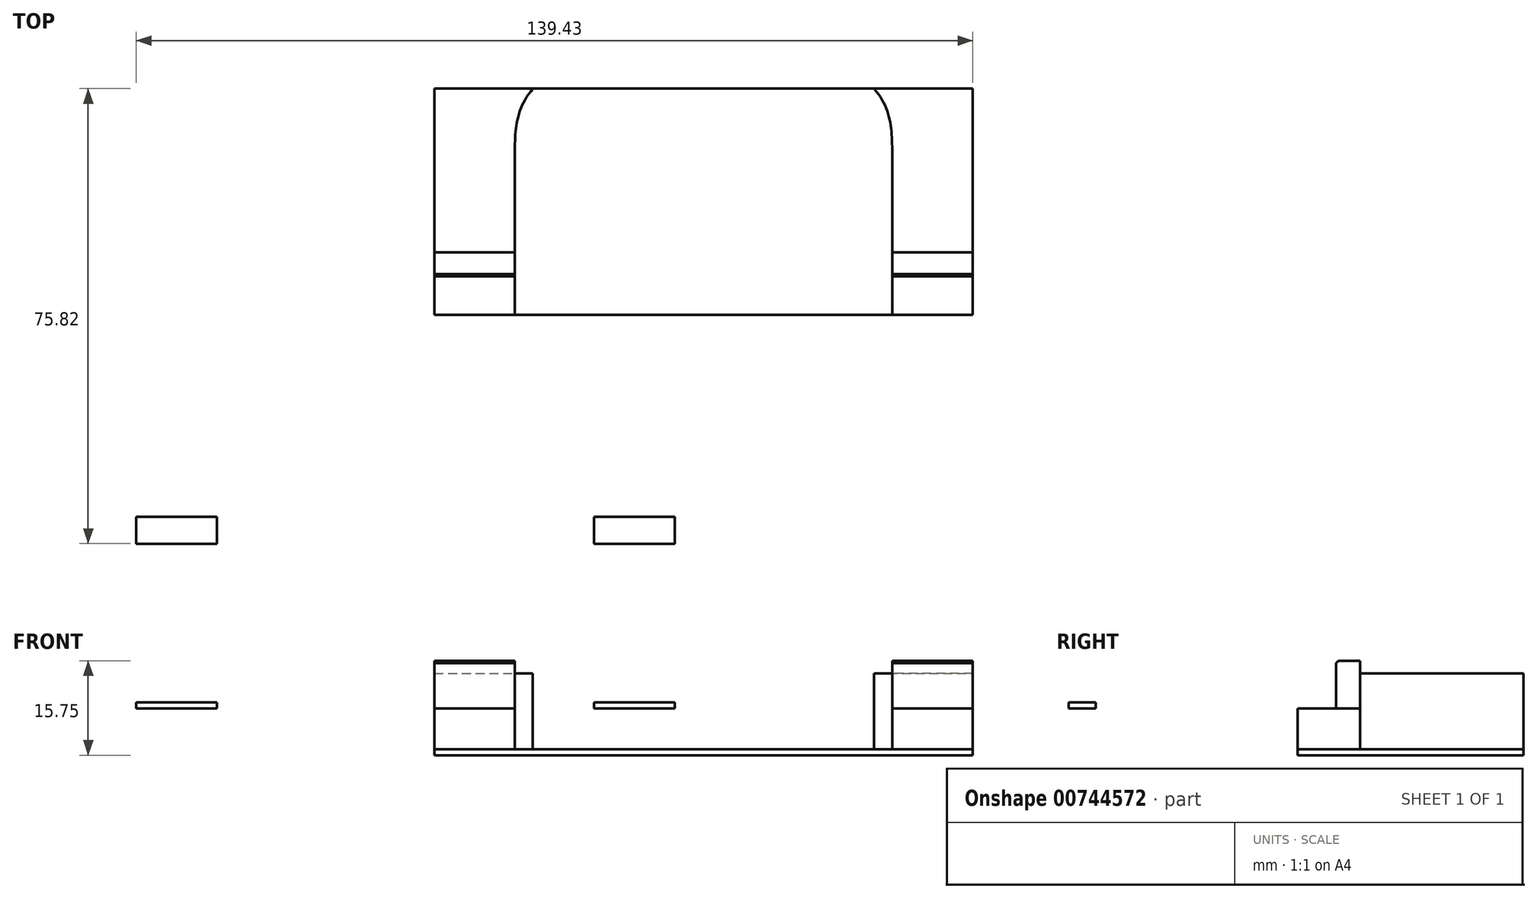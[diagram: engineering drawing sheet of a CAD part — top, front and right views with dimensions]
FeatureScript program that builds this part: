
annotation { "Feature Type Name" : "Feature", "Feature Type Description" : "" }
export const myFeature = defineFeature(function(context is Context, id is Id, definition is map)
    precondition{}
    {
        {
            assignVariable(context, id + "F0", {"name" : "ks_do_riser_height", "anyValue" : 8.95});
        }
        {
            var Q0;
            Q0=qCreatedBy(makeId("Top.planeOp"),FACE);
            var sketch = newSketch(context, id + "F1", { "sketchPlane" : qUnion([Q0])});
            skLineSegment(sketch, "E0", {"start": v(-49.68, -38.15) * mm, "end": v(40.07, -38.15) * mm});
            skPoint(sketch, "E1", {"position": v(-4.8, -38.15) * mm});
            skPoint(sketch, "E2", {"position": v(26.64, -38.15) * mm});
            skPoint(sketch, "E3", {"position": v(-36.26, -38.15) * mm});
            skPoint(sketch, "E4", {"position": v(-49.68, -33.65) * mm});
            skLineSegment(sketch, "E5", {"start": v(-49.68, -38.15) * mm, "end": v(-49.68, -33.65) * mm});
            skLineSegment(sketch, "E6", {"start": v(-49.68, -33.65) * mm, "end": v(-36.26, -33.65) * mm});
            skLineSegment(sketch, "E7", {"start": v(-36.26, -33.65) * mm, "end": v(-36.26, -38.15) * mm});
            skLineSegment(sketch, "E8", {"start": v(26.64, -38.15) * mm, "end": v(26.64, -33.65) * mm});
            skLineSegment(sketch, "E9", {"start": v(26.64, -33.65) * mm, "end": v(40.07, -33.65) * mm});
            skLineSegment(sketch, "E10", {"start": v(40.07, -33.65) * mm, "end": v(40.07, -38.15) * mm});
            skSolve(sketch);
        }
        {
            var Q0;
            {var subQ0=sQuery(id+"F1.wireOp",EDGE,"E5");Q0=makeQuery(id+"F1.imprint","IMPRINT",FACE,{"disambiguationData":[TD([[makeQuery(id+"F1.imprint","IMPRINT",EDGE,{"derivedFrom":subQ0}),-1.0]])]});}
            var Q1;
            {var subQ2=sQuery(id+"F1.wireOp",EDGE,"E8");Q1=makeQuery(id+"F1.imprint","IMPRINT",FACE,{"disambiguationData":[TD([[makeQuery(id+"F1.imprint","IMPRINT",EDGE,{"derivedFrom":subQ2}),-1.0]])]});}
            extrude(context, id + "F2", {"entities" : qUnion([Q0, Q1]), "depth" : 1 * mm, "offsetDistance" : 25 * mm});
        }
        {
            var Q0;
            Q0=makeQuery(id+"F2.opExtrude","CAP_FACE",FACE,{"disambiguationData":[OSD([sQuery(id+"F1.wireOp",EDGE,"E0"),sQuery(id+"F1.wireOp",EDGE,"E5"),sQuery(id+"F1.wireOp",EDGE,"E6"),sQuery(id+"F1.wireOp",EDGE,"E7")])],"isStart":false});
            var sketch = newSketch(context, id + "F3", { "sketchPlane" : qUnion([Q0])});
            skLineSegment(sketch, "E11", {"start": v(-49.68, -38.15) * mm, "end": v(-49.68, -34.15) * mm});
            skLineSegment(sketch, "E12", {"start": v(-49.68, -34.15) * mm, "end": v(-36.26, -34.15) * mm});
            skLineSegment(sketch, "E13", {"start": v(-36.26, -34.15) * mm, "end": v(-36.26, -38.15) * mm});
            skLineSegment(sketch, "E14", {"start": v(-36.26, -38.15) * mm, "end": v(-49.68, -38.15) * mm});
            skPoint(sketch, "E15", {"position": v(40.07, -38.15) * mm});
            skPoint(sketch, "E16", {"position": v(26.64, -34.15) * mm});
            skLineSegment(sketch, "E17.bottom", {"start": v(26.64, -34.15) * mm, "end": v(40.07, -34.15) * mm});
            skLineSegment(sketch, "E17.top", {"start": v(26.64, -38.15) * mm, "end": v(40.07, -38.15) * mm});
            skLineSegment(sketch, "E17.left", {"start": v(26.64, -34.15) * mm, "end": v(26.64, -38.15) * mm});
            skLineSegment(sketch, "E17.right", {"start": v(40.07, -34.15) * mm, "end": v(40.07, -38.15) * mm});
            skSolve(sketch);
        }
        {
            var Q0;
            Q0=makeQuery(id+"F3.imprint","IMPRINT",FACE,{"disambiguationData":[TD([[makeQuery(id+"F3.imprint","IMPRINT",EDGE,{"derivedFrom":sQuery(id+"F3.wireOp",EDGE,"E11")}),-1.0]])]});
            var Q1;
            Q1=makeQuery(id+"F3.imprint","IMPRINT",FACE,{"disambiguationData":[TD([[makeQuery(id+"F3.imprint","IMPRINT",EDGE,{"derivedFrom":sQuery(id+"F3.wireOp",EDGE,"E17.bottom")}),-1.0]])]});
            extrude(context, id + "F4", {"entities" : qUnion([Q0, Q1]), "depth" : (getVariable(context, 'ks_do_riser_height') - 1) * mm, "offsetDistance" : 25 * mm});
        }
        {
            var Q0;
            Q0=makeQuery(id+"F4.opExtrude","CAP_FACE",FACE,{"disambiguationData":[OSD([sQuery(id+"F3.wireOp",EDGE,"E11"),sQuery(id+"F3.wireOp",EDGE,"E12"),sQuery(id+"F3.wireOp",EDGE,"E13"),sQuery(id+"F3.wireOp",EDGE,"E14")])],"isStart":false});
            var sketch = newSketch(context, id + "F5", { "sketchPlane" : qUnion([Q0])});
            skLineSegment(sketch, "E18.bottom", {"start": v(-49.68, -38.15) * mm, "end": v(-36.26, -38.15) * mm});
            skLineSegment(sketch, "E18.top", {"start": v(-49.68, -27.75) * mm, "end": v(-36.26, -27.75) * mm});
            skLineSegment(sketch, "E18.left", {"start": v(-49.68, -38.15) * mm, "end": v(-49.68, -27.75) * mm});
            skLineSegment(sketch, "E18.right", {"start": v(-36.26, -38.15) * mm, "end": v(-36.26, -27.75) * mm});
            skPoint(sketch, "E19", {"position": v(26.64, -38.15) * mm});
            skPoint(sketch, "E20", {"position": v(40.07, -27.75) * mm});
            skLineSegment(sketch, "E21.bottom", {"start": v(26.64, -38.15) * mm, "end": v(40.07, -38.15) * mm});
            skLineSegment(sketch, "E21.top", {"start": v(26.64, -27.75) * mm, "end": v(40.07, -27.75) * mm});
            skLineSegment(sketch, "E21.left", {"start": v(26.64, -38.15) * mm, "end": v(26.64, -27.75) * mm});
            skLineSegment(sketch, "E21.right", {"start": v(40.07, -38.15) * mm, "end": v(40.07, -27.75) * mm});
            skSolve(sketch);
        }
        {
            var Q0;
            Q0=makeQuery(id+"F5.imprint","IMPRINT",FACE,{"disambiguationData":[TD([[makeQuery(id+"F5.imprint","IMPRINT",EDGE,{"derivedFrom":sQuery(id+"F5.wireOp",EDGE,"E21.bottom")}),1.0]])]});
            var Q1;
            {var subQ0=sQuery(id+"F5.wireOp",EDGE,"E18.top");Q1=makeQuery(id+"F5.imprint","IMPRINT",FACE,{"disambiguationData":[TD([[makeQuery(id+"F5.imprint","IMPRINT",EDGE,{"derivedFrom":subQ0}),-1.0]])]});}
            var Q2;
            {var subQ0=sQuery(id+"F5.wireOp",EDGE,"E18.bottom");Q2=makeQuery(id+"F5.imprint","IMPRINT",FACE,{"disambiguationData":[TD([[makeQuery(id+"F5.imprint","IMPRINT",EDGE,{"derivedFrom":subQ0}),1.0]])]});}
            extrude(context, id + "F6", {"entities" : qUnion([Q0, Q1, Q2]), "depth" : 6.8 * mm, "offsetDistance" : 25 * mm});
        }
        {
            var Q0;
            Q0=makeQuery(id+"F6.opExtrude","CAP_FACE",FACE,{"disambiguationData":[OSD([sQuery(id+"F5.wireOp",EDGE,"E18.bottom"),sQuery(id+"F5.wireOp",EDGE,"E18.top"),sQuery(id+"F5.wireOp",EDGE,"E18.left"),sQuery(id+"F5.wireOp",EDGE,"E18.right")])],"isStart":false});
            var sketch = newSketch(context, id + "F7", { "sketchPlane" : qUnion([Q0])});
            skPoint(sketch, "E22", {"position": v(-49.68, -65.42) * mm});
            skPoint(sketch, "E23", {"position": v(40.07, -27.75) * mm});
            skLineSegment(sketch, "E24.bottom", {"start": v(-49.68, -65.42) * mm, "end": v(40.07, -65.42) * mm});
            skLineSegment(sketch, "E24.top", {"start": v(-49.68, -27.75) * mm, "end": v(40.07, -27.75) * mm});
            skLineSegment(sketch, "E24.left", {"start": v(-49.68, -65.42) * mm, "end": v(-49.68, -27.75) * mm});
            skLineSegment(sketch, "E24.right", {"start": v(40.07, -65.42) * mm, "end": v(40.07, -27.75) * mm});
            skSolve(sketch);
        }
        {
            var Q0;
            Q0 = qSketchRegion(id + "F7", true);
            extrude(context, id + "F8", {"entities" : qUnion([Q0]), "depth" : 1 * mm, "offsetDistance" : 25 * mm});
        }
        {
            var Q0;
            Q0=makeQuery(id+"F8.opExtrude","CAP_FACE",FACE,{"disambiguationData":[OSD([sQuery(id+"F7.wireOp",EDGE,"E24.bottom"),sQuery(id+"F7.wireOp",EDGE,"E24.top"),sQuery(id+"F7.wireOp",EDGE,"E24.left"),sQuery(id+"F7.wireOp",EDGE,"E24.right")])],"isStart":true});
            var sketch = newSketch(context, id + "F9", { "sketchPlane" : qUnion([Q0])});
            skPoint(sketch, "E25", {"position": v(26.64, 65.42) * mm});
            skPoint(sketch, "E26", {"position": v(23.64, 65.42) * mm});
            skPoint(sketch, "E27", {"position": v(26.64, 54.25) * mm});
            skPoint(sketch, "E28", {"position": v(40.07, 38.15) * mm});
            skLineSegment(sketch, "E29.bottom", {"start": v(40.07, 38.15) * mm, "end": v(26.64, 38.15) * mm});
            skLineSegment(sketch, "E29.top", {"start": v(40.07, 65.42) * mm, "end": v(26.64, 65.42) * mm});
            skLineSegment(sketch, "E29.left", {"start": v(40.07, 38.15) * mm, "end": v(40.07, 65.42) * mm});
            skLineSegment(sketch, "E29.right", {"start": v(26.64, 38.15) * mm, "end": v(26.64, 65.42) * mm});
            skFitSpline(sketch, "E30", {"points": [v(26.64, 54.25) * mm, v(23.64, 65.42) * mm], "startDerivative": vector(0, 11.66) * mm, "endDerivative": vector(-9, 10.44) * mm});
            skLineSegment(sketch, "E31", {"start": v(-4.8, 27.75) * mm, "end": v(-4.8, 67.87) * mm, "construction": true});
            skLineSegment(sketch, "E32", {"start": v(23.64, 65.42) * mm, "end": v(26.64, 65.42) * mm});
            skFitSpline(sketch, "E33.MirrorCS", {"points": [v(-36.26, 54.25) * mm, v(-33.26, 65.42) * mm], "startDerivative": vector(0, 11.66) * mm, "endDerivative": vector(9, 10.44) * mm});
            skLineSegment(sketch, "E34.MirrorCS", {"start": v(-33.26, 65.42) * mm, "end": v(-36.26, 65.42) * mm});
            skLineSegment(sketch, "E35.MirrorCS", {"start": v(-36.26, 38.15) * mm, "end": v(-36.26, 65.42) * mm});
            skLineSegment(sketch, "E36.MirrorCS", {"start": v(-49.68, 38.15) * mm, "end": v(-49.68, 65.42) * mm});
            skLineSegment(sketch, "E37.MirrorCS", {"start": v(-49.68, 38.15) * mm, "end": v(-36.26, 38.15) * mm});
            skLineSegment(sketch, "E38.MirrorCS", {"start": v(-49.68, 65.42) * mm, "end": v(-36.26, 65.42) * mm});
            skSolve(sketch);
        }
        {
            var Q0;
            Q0=makeQuery(id+"F9.imprint","IMPRINT",FACE,{"disambiguationData":[TD([[makeQuery(id+"F9.imprint","IMPRINT",EDGE,{"derivedFrom":sQuery(id+"F9.wireOp",EDGE,"E36.MirrorCS")}),1.0]])]});
            var Q1;
            {var subQ2=sQuery(id+"F9.wireOp",EDGE,"E30");Q1=makeQuery(id+"F9.imprint","IMPRINT",FACE,{"disambiguationData":[TD([[makeQuery(id+"F9.imprint","IMPRINT",EDGE,{"derivedFrom":subQ2}),-1.0]])]});}
            var Q2;
            {var subQ1=sQuery(id+"F9.wireOp",EDGE,"E29.bottom");Q2=makeQuery(id+"F9.imprint","IMPRINT",FACE,{"disambiguationData":[TD([[makeQuery(id+"F9.imprint","IMPRINT",EDGE,{"derivedFrom":subQ1}),-1.0]])]});}
            var Q3;
            {var subQ0=sQuery(id+"F9.wireOp",EDGE,"E33.MirrorCS");Q3=makeQuery(id+"F9.imprint","IMPRINT",FACE,{"disambiguationData":[TD([[makeQuery(id+"F9.imprint","IMPRINT",EDGE,{"derivedFrom":subQ0}),1.0]])]});}
            extrude(context, id + "F10", {"entities" : qUnion([Q0, Q1, Q2, Q3]), "depth" : 12.6 * mm, "offsetDistance" : 25 * mm});
        }
        {
            var Q0;
            Q0=makeQuery(id+"F4.opExtrude","CAP_EDGE",EDGE,{"disambiguationData":[OSD([sQuery(id+"F3.wireOp",EDGE,"E12")])],"isStart":true});
            chamfer(context, id + "F11", {"entities" : qUnion([Q0]), "width" : 0.4 * mm, "tangentPropagation" : true});
        }
        {
            var Q0;
            Q0=makeQuery(id+"F4.opExtrude","CAP_EDGE",EDGE,{"disambiguationData":[OSD([sQuery(id+"F3.wireOp",EDGE,"E17.bottom")])],"isStart":true});
            chamfer(context, id + "F12", {"entities" : qUnion([Q0]), "width" : 0.4 * mm, "tangentPropagation" : true});
        }
        {
            var Q0;
            Q0=makeQuery(id+"F4.opExtrude","SWEPT_BODY",BODY,{"disambiguationData":[OSD([sQuery(id+"F3.wireOp",EDGE,"E11"),sQuery(id+"F3.wireOp",EDGE,"E12"),sQuery(id+"F3.wireOp",EDGE,"E13"),sQuery(id+"F3.wireOp",EDGE,"E14")])]});
            var Q1;
            Q1=makeQuery(id+"F4.opExtrude","SWEPT_BODY",BODY,{"disambiguationData":[OSD([sQuery(id+"F3.wireOp",EDGE,"E17.bottom"),sQuery(id+"F3.wireOp",EDGE,"E17.top"),sQuery(id+"F3.wireOp",EDGE,"E17.left"),sQuery(id+"F3.wireOp",EDGE,"E17.right")])]});
            var Q2;
            Q2=makeQuery(id+"F6.opExtrude","SWEPT_BODY",BODY,{"disambiguationData":[OSD([sQuery(id+"F5.wireOp",EDGE,"E18.bottom"),sQuery(id+"F5.wireOp",EDGE,"E18.top"),sQuery(id+"F5.wireOp",EDGE,"E18.left"),sQuery(id+"F5.wireOp",EDGE,"E18.right")])]});
            var Q3;
            Q3=makeQuery(id+"F6.opExtrude","SWEPT_BODY",BODY,{"disambiguationData":[OSD([sQuery(id+"F5.wireOp",EDGE,"E21.bottom"),sQuery(id+"F5.wireOp",EDGE,"E21.top"),sQuery(id+"F5.wireOp",EDGE,"E21.left"),sQuery(id+"F5.wireOp",EDGE,"E21.right")])]});
            var Q4;
            Q4=makeQuery(id+"F8.opExtrude","SWEPT_BODY",BODY,{"disambiguationData":[OSD([sQuery(id+"F7.wireOp",EDGE,"E24.bottom"),sQuery(id+"F7.wireOp",EDGE,"E24.top"),sQuery(id+"F7.wireOp",EDGE,"E24.left"),sQuery(id+"F7.wireOp",EDGE,"E24.right")])]});
            var Q5;
            Q5=makeQuery(id+"F10.opExtrude","SWEPT_BODY",BODY,{"disambiguationData":[OSD([sQuery(id+"F9.wireOp",EDGE,"E29.bottom"),sQuery(id+"F9.wireOp",EDGE,"E29.top"),sQuery(id+"F9.wireOp",EDGE,"E29.left"),sQuery(id+"F9.wireOp",EDGE,"E29.right"),sQuery(id+"F9.wireOp",EDGE,"E30"),sQuery(id+"F9.wireOp",EDGE,"E32")])]});
            var Q6;
            Q6=makeQuery(id+"F10.opExtrude","SWEPT_BODY",BODY,{"disambiguationData":[OSD([sQuery(id+"F9.wireOp",EDGE,"E33.MirrorCS"),sQuery(id+"F9.wireOp",EDGE,"E34.MirrorCS"),sQuery(id+"F9.wireOp",EDGE,"E35.MirrorCS"),sQuery(id+"F9.wireOp",EDGE,"E36.MirrorCS"),sQuery(id+"F9.wireOp",EDGE,"E37.MirrorCS"),sQuery(id+"F9.wireOp",EDGE,"E38.MirrorCS")])]});
            var Q7;
            Q7=makeQuery(id+"F8.opExtrude","CAP_EDGE",EDGE,{"disambiguationData":[OSD([sQuery(id+"F7.wireOp",EDGE,"E24.top")])],"isStart":false});
            transform(context, id + "F13", {"entities" : qUnion([Q0, Q1, Q2, Q3, Q4, Q5, Q6]), "transformType" : TransformType.ROTATION, "transformAxis" : qUnion([Q7]), "angle" : 180 * degree, "makeCopy" : false});
        }
        {
            var Q0;
            Q0=makeQuery(id+"F4.opExtrude","SWEPT_BODY",BODY,{"disambiguationData":[OSD([sQuery(id+"F3.wireOp",EDGE,"E11"),sQuery(id+"F3.wireOp",EDGE,"E12"),sQuery(id+"F3.wireOp",EDGE,"E13"),sQuery(id+"F3.wireOp",EDGE,"E14")])]});
            var Q1;
            Q1=makeQuery(id+"F4.opExtrude","SWEPT_BODY",BODY,{"disambiguationData":[OSD([sQuery(id+"F3.wireOp",EDGE,"E17.bottom"),sQuery(id+"F3.wireOp",EDGE,"E17.top"),sQuery(id+"F3.wireOp",EDGE,"E17.left"),sQuery(id+"F3.wireOp",EDGE,"E17.right")])]});
            var Q2;
            Q2=makeQuery(id+"F6.opExtrude","SWEPT_BODY",BODY,{"disambiguationData":[OSD([sQuery(id+"F5.wireOp",EDGE,"E18.bottom"),sQuery(id+"F5.wireOp",EDGE,"E18.top"),sQuery(id+"F5.wireOp",EDGE,"E18.left"),sQuery(id+"F5.wireOp",EDGE,"E18.right")])]});
            var Q3;
            Q3=makeQuery(id+"F6.opExtrude","SWEPT_BODY",BODY,{"disambiguationData":[OSD([sQuery(id+"F5.wireOp",EDGE,"E21.bottom"),sQuery(id+"F5.wireOp",EDGE,"E21.top"),sQuery(id+"F5.wireOp",EDGE,"E21.left"),sQuery(id+"F5.wireOp",EDGE,"E21.right")])]});
            var Q4;
            Q4=makeQuery(id+"F8.opExtrude","SWEPT_BODY",BODY,{"disambiguationData":[OSD([sQuery(id+"F7.wireOp",EDGE,"E24.bottom"),sQuery(id+"F7.wireOp",EDGE,"E24.top"),sQuery(id+"F7.wireOp",EDGE,"E24.left"),sQuery(id+"F7.wireOp",EDGE,"E24.right")])]});
            var Q5;
            Q5=makeQuery(id+"F10.opExtrude","SWEPT_BODY",BODY,{"disambiguationData":[OSD([sQuery(id+"F9.wireOp",EDGE,"E29.bottom"),sQuery(id+"F9.wireOp",EDGE,"E29.top"),sQuery(id+"F9.wireOp",EDGE,"E29.left"),sQuery(id+"F9.wireOp",EDGE,"E29.right"),sQuery(id+"F9.wireOp",EDGE,"E30"),sQuery(id+"F9.wireOp",EDGE,"E32")])]});
            var Q6;
            Q6=makeQuery(id+"F10.opExtrude","SWEPT_BODY",BODY,{"disambiguationData":[OSD([sQuery(id+"F9.wireOp",EDGE,"E33.MirrorCS"),sQuery(id+"F9.wireOp",EDGE,"E34.MirrorCS"),sQuery(id+"F9.wireOp",EDGE,"E35.MirrorCS"),sQuery(id+"F9.wireOp",EDGE,"E36.MirrorCS"),sQuery(id+"F9.wireOp",EDGE,"E37.MirrorCS"),sQuery(id+"F9.wireOp",EDGE,"E38.MirrorCS")])]});
            var Q7;
            Q7=makeQuery(id+"F6.opExtrude","CAP_VERTEX",VERTEX,{"disambiguationData":[OSD([sQuery(id+"F5.wireOp",EDGE,"E18.top"),sQuery(id+"F5.wireOp",EDGE,"E18.left")])],"isStart":true});
            var Q8;
            Q8=qCreatedBy(makeId("Origin.pointOp"),VERTEX);
            transform(context, id + "F14", {"entities" : qUnion([Q0, Q1, Q2, Q3, Q4, Q5, Q6]), "transformType" : TransformType.TRANSLATION_ENTITY, "oppositeDirectionEntity" : false, "transformLine" : qUnion([Q7, Q8]), "makeCopy" : false});
        }
    });
